# Revit family: PRD_FrankeWS_SnkMnlWtrSpplSts_SIRIUSHandBrush_ZSIRW003
name_source: partatom
category: Specialty Equipment
revit_build: Autodesk Revit 2018 (Build: 20190510_1515(x64)
units: mm (PartAtom-declared; Revit-internal decimal feet)

## family parameters
Always vertical = No
Cut with Voids When Loaded = No
OmniClass Number = 23.45.55.11
OmniClass Title = Sanitary Components
Part Type = Normal
Room Calculation Point = No
Round Connector Dimension = Use Diameter
Shared = Yes
Work Plane-Based = Yes

## types (1)
- ZSIRW003
    AssetType = Fixed
    BIMObjectName = PRD_AR_SinkManualWaterSupplySets_SIRIUSHandBrush_ZSIRW003
    Category = Pr_40_20_87_82, Sink manual water supply sets
    Default Elevation = 1219 mm
    Description = Handbrush with lever valve, spray tube with 3 separately mounted brush elements, with connection hose DN 8, G 1/2, length 1400 mm and twist protection.
    DurationUnit = year
    Features = length 1400 mm
    GrossWeight = 1.00 kg
    IfcExportAs = IfcSanitaryTerminalType
    IfcExportType = USERDEFINED
    Manufacturer = KWC Group AG
    ManufacturerName = KWC Group AG
    ManufacturerURL = www.kwc.com
    Model = ZSIRW003
    ModelNumber = 2000101473
    ModelReference = ZSIRW003
    NBSDescription = Water supply fittings for sinks
    NBSReference = 45-35-70/345
    Name = SIRIUS Hand brush ZSIRW003
    NetWeight = 0.88 kg
    NominalDepth = 0 mm  [stored 0 ft]
    NominalHeight = 0 mm  [stored 0 ft]
    NominalLength = 0 mm  [stored 0 ft]
    NominalWidth = 0 mm  [stored 0 ft]
    ProductInformation = https://pim.kwc.com
    Quantity = 1
    QuantityUom = Piece
    Status = New
    URL = www.kwc.com
    Uniclass2015Code = Pr_40_20_87_82
    Uniclass2015Title = Sink manual water supply sets
    Uniclass2015Version = Products v1.23
    Version = 1
    WarrantyDurationUnit = year

note: [stored X ft] marks values corroborated as IEEE doubles in the binary element streams (Revit-internal decimal feet)

## geometry (parser evidence)
native form markers: Sweep x1
no freeform markers — native parametric forms only
